# Revit family: RN 22150 Valvola di distribuzione
name_source: partatom
category: Rohrzubehör
units: mm (PartAtom-declared; Revit-internal decimal feet)

## family parameters
Arbeitsebenenbasiert = Nein
Beim Laden mit Abzugskörper schneiden = Nein
Bemaßung runder Anschluss = Durchmesser verwenden
Gemeinsam genutzt = Nein
Immer vertikal = Ja
Teiletyp = Ventil - Zerlegung in

## types (19) — shared parameters
1.010.00.2 Blattnummer der Richtlinie = 17
1.010.00.3 Ausgabedatum (Monat) der Richtlinie = 201601
1.010.00.4 Herstellername = R. Nussbaum AG
1.010.00.5 Revisionsdatum der Datei = 20190528
1.010.00.6 Webadresse des Herstellers = http://www.nussbaum.ch
1.100.00.3 Sortiernummer für Anzeigereihenfolge = 1
1.100.00.4 Produktbezeichnung = Absperrarmaturen
1.960/3L.00.8 Link (URL) = https://www.nussbaum.ch
17.700.00.4 Armaturentyp = 1
17.700.00.7 Maximale Betriebstemperatur TB [°C] = 90
17.700.00.8 Maximaler Betriebsdruck (Arbeitsdruck) ps [1.0 · 105 Pa] = 16
Connector Visibility = Nein
EnclosingSpace Visibility = Nein
Hersteller = R. Nussbauzm AG
URL = https://www.nussbaum.ch

## per-type parameters (varying)
- DN 25 3: 1.800.00.3 TGA-Nummer=00106000000000000000000000000200700000000000000001???00000; 1.810.00.3 Hersteller-Bestellnummer=22150.41; 1.810.00.4 DATANORM-Nummer=22150.41; 1.810.00.5 StLB-Nummer=622.135; 1.810.00.6 GTIN-Nummer=7612945728890; 17.700.00.30 Produktbeschreibung=22150.41, Batterieventil, ohne Anschlussverschraubung, DN=25, Rp=1; 17.700.00.5 Nennweite DN=25; 17.700.00.6 kvs-Wert [m3/h]=22.84; CONNECTOR0_DIAMETER_dX_0r=25 mm  [stored 0.082021 ft]; CONNECTOR0_dX_00=37 mm; CONNECTOR0_dX_01=20 mm; CONNECTOR0_ref_dX=20 mm; CONNECTOR1_DIAMETER_dX_0r=25 mm  [stored 0.082021 ft]; CONNECTOR1_dX_00=20 mm; CONNECTOR1_dX_01=37 mm; CONNECTOR1_ref_dX=20 mm; CONNECTOR2_DIAMETER_dZ_0r=25 mm  [stored 0.082021 ft]; CONNECTOR2_dZ_00=48 mm; CONNECTOR2_dZ_01=60 mm; CONNECTOR2_ref_dZ=48 mm; Modell=22150.41; R. Nussbaum AG 22150.40 de Visibility=Nein; R. Nussbaum AG 22150.41 de Visibility=Ja; R. Nussbaum AG 22150.42 de Visibility=Nein; R. Nussbaum AG 22150.43 de Visibility=Nein; R. Nussbaum AG 22150.44 de Visibility=Nein; R. Nussbaum AG 22150.45 de Visibility=Nein; R. Nussbaum AG 22150.46 de Visibility=Nein; R. Nussbaum AG 22150.47 de Visibility=Nein; R. Nussbaum AG 22150.48 de Visibility=Nein; R. Nussbaum AG 22150.49 de Visibility=Nein; R. Nussbaum AG 22150.50 de Visibility=Nein; R. Nussbaum AG 22150.51 de Visibility=Nein; R. Nussbaum AG 22150.52 de Visibility=Nein; R. Nussbaum AG 22150.53 de Visibility=Nein; R. Nussbaum AG 22150.54 de Visibility=Nein; R. Nussbaum AG 22150.55 de Visibility=Nein; R. Nussbaum AG 22150.56 de Visibility=Nein; R. Nussbaum AG 22150.57 de Visibility=Nein; R. Nussbaum AG 22150.58 de Visibility=Nein; Typenkommentare=Valvola di distribuzioneDN 25 3
- DN 20: 1.800.00.3 TGA-Nummer=00106000000000000000000000000200700000000000000002???00000; 1.810.00.3 Hersteller-Bestellnummer=22150.42; 1.810.00.4 DATANORM-Nummer=22150.42; 1.810.00.5 StLB-Nummer=622.116; 1.810.00.6 GTIN-Nummer=7612945728852; 17.700.00.30 Produktbeschreibung=22150.42, Batterieventil, ohne Anschlussverschraubung, DN=20, Rp=1¼; 17.700.00.5 Nennweite DN=20; 17.700.00.6 kvs-Wert [m3/h]=16; CONNECTOR0_DIAMETER_dX_0r=32 mm; CONNECTOR0_dX_00=44 mm; CONNECTOR0_dX_01=25 mm  [stored 0.082021 ft]; CONNECTOR0_ref_dX=25 mm  [stored 0.082021 ft]; CONNECTOR1_DIAMETER_dX_0r=32 mm; CONNECTOR1_dX_00=25 mm  [stored 0.082021 ft]; CONNECTOR1_dX_01=44 mm; CONNECTOR1_ref_dX=25 mm  [stored 0.082021 ft]; CONNECTOR2_DIAMETER_dZ_0r=20 mm; CONNECTOR2_dZ_00=50 mm; CONNECTOR2_dZ_01=62 mm  [stored 0.203412 ft]; CONNECTOR2_ref_dZ=50 mm; Modell=22150.42; R. Nussbaum AG 22150.40 de Visibility=Nein; R. Nussbaum AG 22150.41 de Visibility=Nein; R. Nussbaum AG 22150.42 de Visibility=Ja; R. Nussbaum AG 22150.43 de Visibility=Nein; R. Nussbaum AG 22150.44 de Visibility=Nein; R. Nussbaum AG 22150.45 de Visibility=Nein; R. Nussbaum AG 22150.46 de Visibility=Nein; R. Nussbaum AG 22150.47 de Visibility=Nein; R. Nussbaum AG 22150.48 de Visibility=Nein; R. Nussbaum AG 22150.49 de Visibility=Nein; R. Nussbaum AG 22150.50 de Visibility=Nein; R. Nussbaum AG 22150.51 de Visibility=Nein; R. Nussbaum AG 22150.52 de Visibility=Nein; R. Nussbaum AG 22150.53 de Visibility=Nein; R. Nussbaum AG 22150.54 de Visibility=Nein; R. Nussbaum AG 22150.55 de Visibility=Nein; R. Nussbaum AG 22150.56 de Visibility=Nein; R. Nussbaum AG 22150.57 de Visibility=Nein; R. Nussbaum AG 22150.58 de Visibility=Nein; Typenkommentare=Valvola di distribuzioneDN 20
- DN 25 1: 1.800.00.3 TGA-Nummer=00106000000000000000000000000200700000000000000003???00000; 1.810.00.3 Hersteller-Bestellnummer=22150.43; 1.810.00.4 DATANORM-Nummer=22150.43; 1.810.00.5 StLB-Nummer=622.136; 1.810.00.6 GTIN-Nummer=7612945728906; 17.700.00.30 Produktbeschreibung=22150.43, Batterieventil, ohne Anschlussverschraubung, DN=25, Rp=1¼; 17.700.00.5 Nennweite DN=25; 17.700.00.6 kvs-Wert [m3/h]=18.58; CONNECTOR0_DIAMETER_dX_0r=32 mm; CONNECTOR0_dX_00=44 mm; CONNECTOR0_dX_01=25 mm  [stored 0.082021 ft]; CONNECTOR0_ref_dX=25 mm  [stored 0.082021 ft]; CONNECTOR1_DIAMETER_dX_0r=32 mm; CONNECTOR1_dX_00=25 mm  [stored 0.082021 ft]; CONNECTOR1_dX_01=44 mm; CONNECTOR1_ref_dX=25 mm  [stored 0.082021 ft]; CONNECTOR2_DIAMETER_dZ_0r=25 mm  [stored 0.082021 ft]; CONNECTOR2_dZ_00=50 mm; CONNECTOR2_dZ_01=62 mm  [stored 0.203412 ft]; CONNECTOR2_ref_dZ=50 mm; Modell=22150.43; R. Nussbaum AG 22150.40 de Visibility=Nein; R. Nussbaum AG 22150.41 de Visibility=Nein; R. Nussbaum AG 22150.42 de Visibility=Nein; R. Nussbaum AG 22150.43 de Visibility=Ja; R. Nussbaum AG 22150.44 de Visibility=Nein; R. Nussbaum AG 22150.45 de Visibility=Nein; R. Nussbaum AG 22150.46 de Visibility=Nein; R. Nussbaum AG 22150.47 de Visibility=Nein; R. Nussbaum AG 22150.48 de Visibility=Nein; R. Nussbaum AG 22150.49 de Visibility=Nein; R. Nussbaum AG 22150.50 de Visibility=Nein; R. Nussbaum AG 22150.51 de Visibility=Nein; R. Nussbaum AG 22150.52 de Visibility=Nein; R. Nussbaum AG 22150.53 de Visibility=Nein; R. Nussbaum AG 22150.54 de Visibility=Nein; R. Nussbaum AG 22150.55 de Visibility=Nein; R. Nussbaum AG 22150.56 de Visibility=Nein; R. Nussbaum AG 22150.57 de Visibility=Nein; R. Nussbaum AG 22150.58 de Visibility=Nein; Typenkommentare=Valvola di distribuzioneDN 25 1
- DN 32 2: 1.800.00.3 TGA-Nummer=00106000000000000000000000000200700000000000000004???00000; 1.810.00.3 Hersteller-Bestellnummer=22150.44; 1.810.00.4 DATANORM-Nummer=22150.44; 1.810.00.5 StLB-Nummer=622.156; 1.810.00.6 GTIN-Nummer=7612945728869; 17.700.00.30 Produktbeschreibung=22150.44, Batterieventil, ohne Anschlussverschraubung, DN=32, Rp=1¼; 17.700.00.5 Nennweite DN=32; 17.700.00.6 kvs-Wert [m3/h]=43.05; CONNECTOR0_DIAMETER_dX_0r=32 mm; CONNECTOR0_dX_00=44 mm; CONNECTOR0_dX_01=25 mm  [stored 0.082021 ft]; CONNECTOR0_ref_dX=25 mm  [stored 0.082021 ft]; CONNECTOR1_DIAMETER_dX_0r=32 mm; CONNECTOR1_dX_00=25 mm  [stored 0.082021 ft]; CONNECTOR1_dX_01=44 mm; CONNECTOR1_ref_dX=25 mm  [stored 0.082021 ft]; CONNECTOR2_DIAMETER_dZ_0r=32 mm; CONNECTOR2_dZ_00=49 mm; CONNECTOR2_dZ_01=62 mm  [stored 0.203412 ft]; CONNECTOR2_ref_dZ=49 mm; Modell=22150.44; R. Nussbaum AG 22150.40 de Visibility=Nein; R. Nussbaum AG 22150.41 de Visibility=Nein; R. Nussbaum AG 22150.42 de Visibility=Nein; R. Nussbaum AG 22150.43 de Visibility=Nein; R. Nussbaum AG 22150.44 de Visibility=Ja; R. Nussbaum AG 22150.45 de Visibility=Nein; R. Nussbaum AG 22150.46 de Visibility=Nein; R. Nussbaum AG 22150.47 de Visibility=Nein; R. Nussbaum AG 22150.48 de Visibility=Nein; R. Nussbaum AG 22150.49 de Visibility=Nein; R. Nussbaum AG 22150.50 de Visibility=Nein; R. Nussbaum AG 22150.51 de Visibility=Nein; R. Nussbaum AG 22150.52 de Visibility=Nein; R. Nussbaum AG 22150.53 de Visibility=Nein; R. Nussbaum AG 22150.54 de Visibility=Nein; R. Nussbaum AG 22150.55 de Visibility=Nein; R. Nussbaum AG 22150.56 de Visibility=Nein; R. Nussbaum AG 22150.57 de Visibility=Nein; R. Nussbaum AG 22150.58 de Visibility=Nein; Typenkommentare=Valvola di distribuzioneDN 32 2
- DN 20 1: 1.800.00.3 TGA-Nummer=00106000000000000000000000000200700000000000000005???00000; 1.810.00.3 Hersteller-Bestellnummer=22150.45; 1.810.00.4 DATANORM-Nummer=22150.45; 1.810.00.5 StLB-Nummer=622.117; 1.810.00.6 GTIN-Nummer=7612945728913; 17.700.00.30 Produktbeschreibung=22150.45, Batterieventil, ohne Anschlussverschraubung, DN=20, Rp=1½; 17.700.00.5 Nennweite DN=20; 17.700.00.6 kvs-Wert [m3/h]=18; CONNECTOR0_DIAMETER_dX_0r=40 mm; CONNECTOR0_dX_00=49 mm; CONNECTOR0_dX_01=30 mm; CONNECTOR0_ref_dX=30 mm; CONNECTOR1_DIAMETER_dX_0r=40 mm; CONNECTOR1_dX_00=30 mm; CONNECTOR1_dX_01=49 mm; CONNECTOR1_ref_dX=30 mm; CONNECTOR2_DIAMETER_dZ_0r=20 mm; CONNECTOR2_dZ_00=52 mm; CONNECTOR2_dZ_01=65 mm; CONNECTOR2_ref_dZ=52 mm; Modell=22150.45; R. Nussbaum AG 22150.40 de Visibility=Nein; R. Nussbaum AG 22150.41 de Visibility=Nein; R. Nussbaum AG 22150.42 de Visibility=Nein; R. Nussbaum AG 22150.43 de Visibility=Nein; R. Nussbaum AG 22150.44 de Visibility=Nein; R. Nussbaum AG 22150.45 de Visibility=Ja; R. Nussbaum AG 22150.46 de Visibility=Nein; R. Nussbaum AG 22150.47 de Visibility=Nein; R. Nussbaum AG 22150.48 de Visibility=Nein; R. Nussbaum AG 22150.49 de Visibility=Nein; R. Nussbaum AG 22150.50 de Visibility=Nein; R. Nussbaum AG 22150.51 de Visibility=Nein; R. Nussbaum AG 22150.52 de Visibility=Nein; R. Nussbaum AG 22150.53 de Visibility=Nein; R. Nussbaum AG 22150.54 de Visibility=Nein; R. Nussbaum AG 22150.55 de Visibility=Nein; R. Nussbaum AG 22150.56 de Visibility=Nein; R. Nussbaum AG 22150.57 de Visibility=Nein; R. Nussbaum AG 22150.58 de Visibility=Nein; Typenkommentare=Valvola di distribuzioneDN 20 1
- DN 25 4: 1.800.00.3 TGA-Nummer=00106000000000000000000000000200700000000000000006???00000; 1.810.00.3 Hersteller-Bestellnummer=22150.46; 1.810.00.4 DATANORM-Nummer=22150.46; 1.810.00.5 StLB-Nummer=622.137; 1.810.00.6 GTIN-Nummer=7612945728876; 17.700.00.30 Produktbeschreibung=22150.46, Batterieventil, ohne Anschlussverschraubung, DN=25, Rp=1½; 17.700.00.5 Nennweite DN=25; 17.700.00.6 kvs-Wert [m3/h]=18; CONNECTOR0_DIAMETER_dX_0r=40 mm; CONNECTOR0_dX_00=49 mm; CONNECTOR0_dX_01=30 mm; CONNECTOR0_ref_dX=30 mm; CONNECTOR1_DIAMETER_dX_0r=40 mm; CONNECTOR1_dX_00=30 mm; CONNECTOR1_dX_01=49 mm; CONNECTOR1_ref_dX=30 mm; CONNECTOR2_DIAMETER_dZ_0r=25 mm  [stored 0.082021 ft]; CONNECTOR2_dZ_00=52 mm; CONNECTOR2_dZ_01=65 mm; CONNECTOR2_ref_dZ=52 mm; Modell=22150.46; R. Nussbaum AG 22150.40 de Visibility=Nein; R. Nussbaum AG 22150.41 de Visibility=Nein; R. Nussbaum AG 22150.42 de Visibility=Nein; R. Nussbaum AG 22150.43 de Visibility=Nein; R. Nussbaum AG 22150.44 de Visibility=Nein; R. Nussbaum AG 22150.45 de Visibility=Nein; R. Nussbaum AG 22150.46 de Visibility=Ja; R. Nussbaum AG 22150.47 de Visibility=Nein; R. Nussbaum AG 22150.48 de Visibility=Nein; R. Nussbaum AG 22150.49 de Visibility=Nein; R. Nussbaum AG 22150.50 de Visibility=Nein; R. Nussbaum AG 22150.51 de Visibility=Nein; R. Nussbaum AG 22150.52 de Visibility=Nein; R. Nussbaum AG 22150.53 de Visibility=Nein; R. Nussbaum AG 22150.54 de Visibility=Nein; R. Nussbaum AG 22150.55 de Visibility=Nein; R. Nussbaum AG 22150.56 de Visibility=Nein; R. Nussbaum AG 22150.57 de Visibility=Nein; R. Nussbaum AG 22150.58 de Visibility=Nein; Typenkommentare=Valvola di distribuzioneDN 25 4
- DN 32 1: 1.800.00.3 TGA-Nummer=00106000000000000000000000000200700000000000000007???00000; 1.810.00.3 Hersteller-Bestellnummer=22150.47; 1.810.00.4 DATANORM-Nummer=22150.47; 1.810.00.5 StLB-Nummer=622.157; 1.810.00.6 GTIN-Nummer=7612945728920; 17.700.00.30 Produktbeschreibung=22150.47, Batterieventil, ohne Anschlussverschraubung, DN=32, Rp=1½; 17.700.00.5 Nennweite DN=32; 17.700.00.6 kvs-Wert [m3/h]=36.27; CONNECTOR0_DIAMETER_dX_0r=40 mm; CONNECTOR0_dX_00=49 mm; CONNECTOR0_dX_01=30 mm; CONNECTOR0_ref_dX=30 mm; CONNECTOR1_DIAMETER_dX_0r=40 mm; CONNECTOR1_dX_00=30 mm; CONNECTOR1_dX_01=49 mm; CONNECTOR1_ref_dX=30 mm; CONNECTOR2_DIAMETER_dZ_0r=32 mm; CONNECTOR2_dZ_00=52 mm; CONNECTOR2_dZ_01=65 mm; CONNECTOR2_ref_dZ=52 mm; Modell=22150.47; R. Nussbaum AG 22150.40 de Visibility=Nein; R. Nussbaum AG 22150.41 de Visibility=Nein; R. Nussbaum AG 22150.42 de Visibility=Nein; R. Nussbaum AG 22150.43 de Visibility=Nein; R. Nussbaum AG 22150.44 de Visibility=Nein; R. Nussbaum AG 22150.45 de Visibility=Nein; R. Nussbaum AG 22150.46 de Visibility=Nein; R. Nussbaum AG 22150.47 de Visibility=Ja; R. Nussbaum AG 22150.48 de Visibility=Nein; R. Nussbaum AG 22150.49 de Visibility=Nein; R. Nussbaum AG 22150.50 de Visibility=Nein; R. Nussbaum AG 22150.51 de Visibility=Nein; R. Nussbaum AG 22150.52 de Visibility=Nein; R. Nussbaum AG 22150.53 de Visibility=Nein; R. Nussbaum AG 22150.54 de Visibility=Nein; R. Nussbaum AG 22150.55 de Visibility=Nein; R. Nussbaum AG 22150.56 de Visibility=Nein; R. Nussbaum AG 22150.57 de Visibility=Nein; R. Nussbaum AG 22150.58 de Visibility=Nein; Typenkommentare=Valvola di distribuzioneDN 32 1
- DN 40 1: 1.800.00.3 TGA-Nummer=00106000000000000000000000000200700000000000000008???00000; 1.810.00.3 Hersteller-Bestellnummer=22150.48; 1.810.00.4 DATANORM-Nummer=22150.48; 1.810.00.5 StLB-Nummer=622.217; 1.810.00.6 GTIN-Nummer=7612945726865; 17.700.00.30 Produktbeschreibung=22150.48, Batterieventil, ohne Anschlussverschraubung, DN=40, Rp=1½; 17.700.00.5 Nennweite DN=40; 17.700.00.6 kvs-Wert [m3/h]=54.13; CONNECTOR0_DIAMETER_dX_0r=40 mm; CONNECTOR0_dX_00=49 mm; CONNECTOR0_dX_01=30 mm; CONNECTOR0_ref_dX=30 mm; CONNECTOR1_DIAMETER_dX_0r=40 mm; CONNECTOR1_dX_00=30 mm; CONNECTOR1_dX_01=49 mm; CONNECTOR1_ref_dX=30 mm; CONNECTOR2_DIAMETER_dZ_0r=40 mm; CONNECTOR2_dZ_00=52 mm; CONNECTOR2_dZ_01=65 mm; CONNECTOR2_ref_dZ=52 mm; Modell=22150.48; R. Nussbaum AG 22150.40 de Visibility=Nein; R. Nussbaum AG 22150.41 de Visibility=Nein; R. Nussbaum AG 22150.42 de Visibility=Nein; R. Nussbaum AG 22150.43 de Visibility=Nein; R. Nussbaum AG 22150.44 de Visibility=Nein; R. Nussbaum AG 22150.45 de Visibility=Nein; R. Nussbaum AG 22150.46 de Visibility=Nein; R. Nussbaum AG 22150.47 de Visibility=Nein; R. Nussbaum AG 22150.48 de Visibility=Ja; R. Nussbaum AG 22150.49 de Visibility=Nein; R. Nussbaum AG 22150.50 de Visibility=Nein; R. Nussbaum AG 22150.51 de Visibility=Nein; R. Nussbaum AG 22150.52 de Visibility=Nein; R. Nussbaum AG 22150.53 de Visibility=Nein; R. Nussbaum AG 22150.54 de Visibility=Nein; R. Nussbaum AG 22150.55 de Visibility=Nein; R. Nussbaum AG 22150.56 de Visibility=Nein; R. Nussbaum AG 22150.57 de Visibility=Nein; R. Nussbaum AG 22150.58 de Visibility=Nein; Typenkommentare=Valvola di distribuzioneDN 40 1
- DN 20 3: 1.800.00.3 TGA-Nummer=00106000000000000000000000000200700000000000000009???00000; 1.810.00.3 Hersteller-Bestellnummer=22150.49; 1.810.00.4 DATANORM-Nummer=22150.49; 1.810.00.5 StLB-Nummer=622.118; 1.810.00.6 GTIN-Nummer=7612945728937; 17.700.00.30 Produktbeschreibung=22150.49, Batterieventil, ohne Anschlussverschraubung, DN=20, Rp=2; 17.700.00.5 Nennweite DN=20; 17.700.00.6 kvs-Wert [m3/h]=30; CONNECTOR0_DIAMETER_dX_0r=50 mm; CONNECTOR0_dX_00=59 mm; CONNECTOR0_dX_01=35 mm  [stored 0.114829 ft]; CONNECTOR0_ref_dX=35 mm  [stored 0.114829 ft]; CONNECTOR1_DIAMETER_dX_0r=50 mm; CONNECTOR1_dX_00=35 mm  [stored 0.114829 ft]; CONNECTOR1_dX_01=59 mm; CONNECTOR1_ref_dX=35 mm  [stored 0.114829 ft]; CONNECTOR2_DIAMETER_dZ_0r=20 mm; CONNECTOR2_dZ_00=60 mm; CONNECTOR2_dZ_01=73 mm  [stored 0.239501 ft]; CONNECTOR2_ref_dZ=60 mm; Modell=22150.49; R. Nussbaum AG 22150.40 de Visibility=Nein; R. Nussbaum AG 22150.41 de Visibility=Nein; R. Nussbaum AG 22150.42 de Visibility=Nein; R. Nussbaum AG 22150.43 de Visibility=Nein; R. Nussbaum AG 22150.44 de Visibility=Nein; R. Nussbaum AG 22150.45 de Visibility=Nein; R. Nussbaum AG 22150.46 de Visibility=Nein; R. Nussbaum AG 22150.47 de Visibility=Nein; R. Nussbaum AG 22150.48 de Visibility=Nein; R. Nussbaum AG 22150.49 de Visibility=Ja; R. Nussbaum AG 22150.50 de Visibility=Nein; R. Nussbaum AG 22150.51 de Visibility=Nein; R. Nussbaum AG 22150.52 de Visibility=Nein; R. Nussbaum AG 22150.53 de Visibility=Nein; R. Nussbaum AG 22150.54 de Visibility=Nein; R. Nussbaum AG 22150.55 de Visibility=Nein; R. Nussbaum AG 22150.56 de Visibility=Nein; R. Nussbaum AG 22150.57 de Visibility=Nein; R. Nussbaum AG 22150.58 de Visibility=Nein; Typenkommentare=Valvola di distribuzioneDN 20 3
- DN 32 3: 1.800.00.3 TGA-Nummer=00106000000000000000000000000200700000000000000010???00000; 1.810.00.3 Hersteller-Bestellnummer=22150.51; 1.810.00.4 DATANORM-Nummer=22150.51; 1.810.00.5 StLB-Nummer=622.158; 1.810.00.6 GTIN-Nummer=7612945728944; 17.700.00.30 Produktbeschreibung=22150.51, Batterieventil, ohne Anschlussverschraubung, DN=32, Rp=2; 17.700.00.5 Nennweite DN=32; 17.700.00.6 kvs-Wert [m3/h]=33.26; CONNECTOR0_DIAMETER_dX_0r=50 mm; CONNECTOR0_dX_00=59 mm; CONNECTOR0_dX_01=35 mm  [stored 0.114829 ft]; CONNECTOR0_ref_dX=35 mm  [stored 0.114829 ft]; CONNECTOR1_DIAMETER_dX_0r=50 mm; CONNECTOR1_dX_00=35 mm  [stored 0.114829 ft]; CONNECTOR1_dX_01=59 mm; CONNECTOR1_ref_dX=35 mm  [stored 0.114829 ft]; CONNECTOR2_DIAMETER_dZ_0r=32 mm; CONNECTOR2_dZ_00=60 mm; CONNECTOR2_dZ_01=73 mm  [stored 0.239501 ft]; CONNECTOR2_ref_dZ=60 mm; Modell=22150.51; R. Nussbaum AG 22150.40 de Visibility=Nein; R. Nussbaum AG 22150.41 de Visibility=Nein; R. Nussbaum AG 22150.42 de Visibility=Nein; R. Nussbaum AG 22150.43 de Visibility=Nein; R. Nussbaum AG 22150.44 de Visibility=Nein; R. Nussbaum AG 22150.45 de Visibility=Nein; R. Nussbaum AG 22150.46 de Visibility=Nein; R. Nussbaum AG 22150.47 de Visibility=Nein; R. Nussbaum AG 22150.48 de Visibility=Nein; R. Nussbaum AG 22150.49 de Visibility=Nein; R. Nussbaum AG 22150.50 de Visibility=Nein; R. Nussbaum AG 22150.51 de Visibility=Ja; R. Nussbaum AG 22150.52 de Visibility=Nein; R. Nussbaum AG 22150.53 de Visibility=Nein; R. Nussbaum AG 22150.54 de Visibility=Nein; R. Nussbaum AG 22150.55 de Visibility=Nein; R. Nussbaum AG 22150.56 de Visibility=Nein; R. Nussbaum AG 22150.57 de Visibility=Nein; R. Nussbaum AG 22150.58 de Visibility=Nein; Typenkommentare=Valvola di distribuzioneDN 32 3
- DN 40 2: 1.800.00.3 TGA-Nummer=00106000000000000000000000000200700000000000000011???00000; 1.810.00.3 Hersteller-Bestellnummer=22150.52; 1.810.00.4 DATANORM-Nummer=22150.52; 1.810.00.5 StLB-Nummer=622.218; 1.810.00.6 GTIN-Nummer=7612945726872; 17.700.00.30 Produktbeschreibung=22150.52, Batterieventil, ohne Anschlussverschraubung, DN=40, Rp=2; 17.700.00.5 Nennweite DN=40; 17.700.00.6 kvs-Wert [m3/h]=50; CONNECTOR0_DIAMETER_dX_0r=50 mm; CONNECTOR0_dX_00=59 mm; CONNECTOR0_dX_01=35 mm  [stored 0.114829 ft]; CONNECTOR0_ref_dX=35 mm  [stored 0.114829 ft]; CONNECTOR1_DIAMETER_dX_0r=50 mm; CONNECTOR1_dX_00=35 mm  [stored 0.114829 ft]; CONNECTOR1_dX_01=59 mm; CONNECTOR1_ref_dX=35 mm  [stored 0.114829 ft]; CONNECTOR2_DIAMETER_dZ_0r=40 mm; CONNECTOR2_dZ_00=60 mm; CONNECTOR2_dZ_01=73 mm  [stored 0.239501 ft]; CONNECTOR2_ref_dZ=60 mm; Modell=22150.52; R. Nussbaum AG 22150.40 de Visibility=Nein; R. Nussbaum AG 22150.41 de Visibility=Nein; R. Nussbaum AG 22150.42 de Visibility=Nein; R. Nussbaum AG 22150.43 de Visibility=Nein; R. Nussbaum AG 22150.44 de Visibility=Nein; R. Nussbaum AG 22150.45 de Visibility=Nein; R. Nussbaum AG 22150.46 de Visibility=Nein; R. Nussbaum AG 22150.47 de Visibility=Nein; R. Nussbaum AG 22150.48 de Visibility=Nein; R. Nussbaum AG 22150.49 de Visibility=Nein; R. Nussbaum AG 22150.50 de Visibility=Nein; R. Nussbaum AG 22150.51 de Visibility=Nein; R. Nussbaum AG 22150.52 de Visibility=Ja; R. Nussbaum AG 22150.53 de Visibility=Nein; R. Nussbaum AG 22150.54 de Visibility=Nein; R. Nussbaum AG 22150.55 de Visibility=Nein; R. Nussbaum AG 22150.56 de Visibility=Nein; R. Nussbaum AG 22150.57 de Visibility=Nein; R. Nussbaum AG 22150.58 de Visibility=Nein; Typenkommentare=Valvola di distribuzioneDN 40 2
- DN 50: 1.800.00.3 TGA-Nummer=00106000000000000000000000000200700000000000000012???00000; 1.810.00.3 Hersteller-Bestellnummer=22150.53; 1.810.00.4 DATANORM-Nummer=22150.53; 1.810.00.5 StLB-Nummer=622.238; 1.810.00.6 GTIN-Nummer=7612945727107; 17.700.00.30 Produktbeschreibung=22150.53, Batterieventil, ohne Anschlussverschraubung, DN=50, Rp=2; 17.700.00.5 Nennweite DN=50; 17.700.00.6 kvs-Wert [m3/h]=82.84; CONNECTOR0_DIAMETER_dX_0r=50 mm; CONNECTOR0_dX_00=59 mm; CONNECTOR0_dX_01=35 mm  [stored 0.114829 ft]; CONNECTOR0_ref_dX=35 mm  [stored 0.114829 ft]; CONNECTOR1_DIAMETER_dX_0r=50 mm; CONNECTOR1_dX_00=35 mm  [stored 0.114829 ft]; CONNECTOR1_dX_01=59 mm; CONNECTOR1_ref_dX=35 mm  [stored 0.114829 ft]; CONNECTOR2_DIAMETER_dZ_0r=50 mm; CONNECTOR2_dZ_00=60 mm; CONNECTOR2_dZ_01=73 mm  [stored 0.239501 ft]; CONNECTOR2_ref_dZ=60 mm; Modell=22150.53; R. Nussbaum AG 22150.40 de Visibility=Nein; R. Nussbaum AG 22150.41 de Visibility=Nein; R. Nussbaum AG 22150.42 de Visibility=Nein; R. Nussbaum AG 22150.43 de Visibility=Nein; R. Nussbaum AG 22150.44 de Visibility=Nein; R. Nussbaum AG 22150.45 de Visibility=Nein; R. Nussbaum AG 22150.46 de Visibility=Nein; R. Nussbaum AG 22150.47 de Visibility=Nein; R. Nussbaum AG 22150.48 de Visibility=Nein; R. Nussbaum AG 22150.49 de Visibility=Nein; R. Nussbaum AG 22150.50 de Visibility=Nein; R. Nussbaum AG 22150.51 de Visibility=Nein; R. Nussbaum AG 22150.52 de Visibility=Nein; R. Nussbaum AG 22150.53 de Visibility=Ja; R. Nussbaum AG 22150.54 de Visibility=Nein; R. Nussbaum AG 22150.55 de Visibility=Nein; R. Nussbaum AG 22150.56 de Visibility=Nein; R. Nussbaum AG 22150.57 de Visibility=Nein; R. Nussbaum AG 22150.58 de Visibility=Nein; Typenkommentare=Valvola di distribuzioneDN 50
- DN 25 2: 1.800.00.3 TGA-Nummer=00106000000000000000000000000200700000000000000013???00000; 1.810.00.3 Hersteller-Bestellnummer=22150.54; 1.810.00.4 DATANORM-Nummer=22150.54; 1.810.00.5 StLB-Nummer=622.141; 1.810.00.6 GTIN-Nummer=7612945726889; 17.700.00.30 Produktbeschreibung=22150.54, Batterieventil, ohne Anschlussverschraubung, DN=25, Rp=2½; 17.700.00.5 Nennweite DN=25; 17.700.00.6 kvs-Wert [m3/h]=38; CONNECTOR0_DIAMETER_dX_0r=65 mm; CONNECTOR0_dX_00=62 mm  [stored 0.203412 ft]; CONNECTOR0_dX_01=35 mm  [stored 0.114829 ft]; CONNECTOR0_ref_dX=35 mm  [stored 0.114829 ft]; CONNECTOR1_DIAMETER_dX_0r=65 mm; CONNECTOR1_dX_00=35 mm  [stored 0.114829 ft]; CONNECTOR1_dX_01=62 mm  [stored 0.203412 ft]; CONNECTOR1_ref_dX=35 mm  [stored 0.114829 ft]; CONNECTOR2_DIAMETER_dZ_0r=25 mm  [stored 0.082021 ft]; CONNECTOR2_dZ_00=70 mm; CONNECTOR2_dZ_01=83 mm; CONNECTOR2_ref_dZ=70 mm; Modell=22150.54; R. Nussbaum AG 22150.40 de Visibility=Nein; R. Nussbaum AG 22150.41 de Visibility=Nein; R. Nussbaum AG 22150.42 de Visibility=Nein; R. Nussbaum AG 22150.43 de Visibility=Nein; R. Nussbaum AG 22150.44 de Visibility=Nein; R. Nussbaum AG 22150.45 de Visibility=Nein; R. Nussbaum AG 22150.46 de Visibility=Nein; R. Nussbaum AG 22150.47 de Visibility=Nein; R. Nussbaum AG 22150.48 de Visibility=Nein; R. Nussbaum AG 22150.49 de Visibility=Nein; R. Nussbaum AG 22150.50 de Visibility=Nein; R. Nussbaum AG 22150.51 de Visibility=Nein; R. Nussbaum AG 22150.52 de Visibility=Nein; R. Nussbaum AG 22150.53 de Visibility=Nein; R. Nussbaum AG 22150.54 de Visibility=Ja; R. Nussbaum AG 22150.55 de Visibility=Nein; R. Nussbaum AG 22150.56 de Visibility=Nein; R. Nussbaum AG 22150.57 de Visibility=Nein; R. Nussbaum AG 22150.58 de Visibility=Nein; Typenkommentare=Valvola di distribuzioneDN 25 2
- DN 32: 1.800.00.3 TGA-Nummer=00106000000000000000000000000200700000000000000014???00000; 1.810.00.3 Hersteller-Bestellnummer=22150.55; 1.810.00.4 DATANORM-Nummer=22150.55; 1.810.00.5 StLB-Nummer=622.161; 1.810.00.6 GTIN-Nummer=7612945727114; 17.700.00.30 Produktbeschreibung=22150.55, Batterieventil, ohne Anschlussverschraubung, DN=32, Rp=2½; 17.700.00.5 Nennweite DN=32; 17.700.00.6 kvs-Wert [m3/h]=33.56; CONNECTOR0_DIAMETER_dX_0r=65 mm; CONNECTOR0_dX_00=62 mm  [stored 0.203412 ft]; CONNECTOR0_dX_01=35 mm  [stored 0.114829 ft]; CONNECTOR0_ref_dX=35 mm  [stored 0.114829 ft]; CONNECTOR1_DIAMETER_dX_0r=65 mm; CONNECTOR1_dX_00=35 mm  [stored 0.114829 ft]; CONNECTOR1_dX_01=62 mm  [stored 0.203412 ft]; CONNECTOR1_ref_dX=35 mm  [stored 0.114829 ft]; CONNECTOR2_DIAMETER_dZ_0r=32 mm; CONNECTOR2_dZ_00=70 mm; CONNECTOR2_dZ_01=83 mm; CONNECTOR2_ref_dZ=70 mm; Modell=22150.55; R. Nussbaum AG 22150.40 de Visibility=Nein; R. Nussbaum AG 22150.41 de Visibility=Nein; R. Nussbaum AG 22150.42 de Visibility=Nein; R. Nussbaum AG 22150.43 de Visibility=Nein; R. Nussbaum AG 22150.44 de Visibility=Nein; R. Nussbaum AG 22150.45 de Visibility=Nein; R. Nussbaum AG 22150.46 de Visibility=Nein; R. Nussbaum AG 22150.47 de Visibility=Nein; R. Nussbaum AG 22150.48 de Visibility=Nein; R. Nussbaum AG 22150.49 de Visibility=Nein; R. Nussbaum AG 22150.50 de Visibility=Nein; R. Nussbaum AG 22150.51 de Visibility=Nein; R. Nussbaum AG 22150.52 de Visibility=Nein; R. Nussbaum AG 22150.53 de Visibility=Nein; R. Nussbaum AG 22150.54 de Visibility=Nein; R. Nussbaum AG 22150.55 de Visibility=Ja; R. Nussbaum AG 22150.56 de Visibility=Nein; R. Nussbaum AG 22150.57 de Visibility=Nein; R. Nussbaum AG 22150.58 de Visibility=Nein; Typenkommentare=Valvola di distribuzioneDN 32
- DN 40: 1.800.00.3 TGA-Nummer=00106000000000000000000000000200700000000000000015???00000; 1.810.00.3 Hersteller-Bestellnummer=22150.56; 1.810.00.4 DATANORM-Nummer=22150.56; 1.810.00.5 StLB-Nummer=622.221; 1.810.00.6 GTIN-Nummer=7612945726896; 17.700.00.30 Produktbeschreibung=22150.56, Batterieventil, ohne Anschlussverschraubung, DN=40, Rp=2½; 17.700.00.5 Nennweite DN=40; 17.700.00.6 kvs-Wert [m3/h]=55; CONNECTOR0_DIAMETER_dX_0r=65 mm; CONNECTOR0_dX_00=62 mm  [stored 0.203412 ft]; CONNECTOR0_dX_01=35 mm  [stored 0.114829 ft]; CONNECTOR0_ref_dX=35 mm  [stored 0.114829 ft]; CONNECTOR1_DIAMETER_dX_0r=65 mm; CONNECTOR1_dX_00=35 mm  [stored 0.114829 ft]; CONNECTOR1_dX_01=62 mm  [stored 0.203412 ft]; CONNECTOR1_ref_dX=35 mm  [stored 0.114829 ft]; CONNECTOR2_DIAMETER_dZ_0r=40 mm; CONNECTOR2_dZ_00=70 mm; CONNECTOR2_dZ_01=83 mm; CONNECTOR2_ref_dZ=70 mm; Modell=22150.56; R. Nussbaum AG 22150.40 de Visibility=Nein; R. Nussbaum AG 22150.41 de Visibility=Nein; R. Nussbaum AG 22150.42 de Visibility=Nein; R. Nussbaum AG 22150.43 de Visibility=Nein; R. Nussbaum AG 22150.44 de Visibility=Nein; R. Nussbaum AG 22150.45 de Visibility=Nein; R. Nussbaum AG 22150.46 de Visibility=Nein; R. Nussbaum AG 22150.47 de Visibility=Nein; R. Nussbaum AG 22150.48 de Visibility=Nein; R. Nussbaum AG 22150.49 de Visibility=Nein; R. Nussbaum AG 22150.50 de Visibility=Nein; R. Nussbaum AG 22150.51 de Visibility=Nein; R. Nussbaum AG 22150.52 de Visibility=Nein; R. Nussbaum AG 22150.53 de Visibility=Nein; R. Nussbaum AG 22150.54 de Visibility=Nein; R. Nussbaum AG 22150.55 de Visibility=Nein; R. Nussbaum AG 22150.56 de Visibility=Ja; R. Nussbaum AG 22150.57 de Visibility=Nein; R. Nussbaum AG 22150.58 de Visibility=Nein; Typenkommentare=Valvola di distribuzioneDN 40
- DN 50 1: 1.800.00.3 TGA-Nummer=00106000000000000000000000000200700000000000000016???00000; 1.810.00.3 Hersteller-Bestellnummer=22150.57; 1.810.00.4 DATANORM-Nummer=22150.57; 1.810.00.5 StLB-Nummer=622.241; 1.810.00.6 GTIN-Nummer=7612945727121; 17.700.00.30 Produktbeschreibung=22150.57, Batterieventil, ohne Anschlussverschraubung, DN=50, Rp=2½; 17.700.00.5 Nennweite DN=50; 17.700.00.6 kvs-Wert [m3/h]=72.18; CONNECTOR0_DIAMETER_dX_0r=65 mm; CONNECTOR0_dX_00=62 mm  [stored 0.203412 ft]; CONNECTOR0_dX_01=35 mm  [stored 0.114829 ft]; CONNECTOR0_ref_dX=35 mm  [stored 0.114829 ft]; CONNECTOR1_DIAMETER_dX_0r=65 mm; CONNECTOR1_dX_00=35 mm  [stored 0.114829 ft]; CONNECTOR1_dX_01=62 mm  [stored 0.203412 ft]; CONNECTOR1_ref_dX=35 mm  [stored 0.114829 ft]; CONNECTOR2_DIAMETER_dZ_0r=50 mm; CONNECTOR2_dZ_00=70 mm; CONNECTOR2_dZ_01=83 mm; CONNECTOR2_ref_dZ=70 mm; Modell=22150.57; R. Nussbaum AG 22150.40 de Visibility=Nein; R. Nussbaum AG 22150.41 de Visibility=Nein; R. Nussbaum AG 22150.42 de Visibility=Nein; R. Nussbaum AG 22150.43 de Visibility=Nein; R. Nussbaum AG 22150.44 de Visibility=Nein; R. Nussbaum AG 22150.45 de Visibility=Nein; R. Nussbaum AG 22150.46 de Visibility=Nein; R. Nussbaum AG 22150.47 de Visibility=Nein; R. Nussbaum AG 22150.48 de Visibility=Nein; R. Nussbaum AG 22150.49 de Visibility=Nein; R. Nussbaum AG 22150.50 de Visibility=Nein; R. Nussbaum AG 22150.51 de Visibility=Nein; R. Nussbaum AG 22150.52 de Visibility=Nein; R. Nussbaum AG 22150.53 de Visibility=Nein; R. Nussbaum AG 22150.54 de Visibility=Nein; R. Nussbaum AG 22150.55 de Visibility=Nein; R. Nussbaum AG 22150.56 de Visibility=Nein; R. Nussbaum AG 22150.57 de Visibility=Ja; R. Nussbaum AG 22150.58 de Visibility=Nein; Typenkommentare=Valvola di distribuzioneDN 50 1
- DN 25: 1.800.00.3 TGA-Nummer=00106000000000000000000000000200700000000000000017???00000; 1.810.00.3 Hersteller-Bestellnummer=22150.5; 1.810.00.4 DATANORM-Nummer=22150.5; 1.810.00.5 StLB-Nummer=622.138; 1.810.00.6 GTIN-Nummer=7612945728883; 17.700.00.30 Produktbeschreibung=22150.50, Batterieventil, ohne Anschlussverschraubung, DN=25, Rp=2; 17.700.00.5 Nennweite DN=25; 17.700.00.6 kvs-Wert [m3/h]=31; CONNECTOR0_DIAMETER_dX_0r=50 mm; CONNECTOR0_dX_00=59 mm; CONNECTOR0_dX_01=35 mm  [stored 0.114829 ft]; CONNECTOR0_ref_dX=35 mm  [stored 0.114829 ft]; CONNECTOR1_DIAMETER_dX_0r=50 mm; CONNECTOR1_dX_00=35 mm  [stored 0.114829 ft]; CONNECTOR1_dX_01=59 mm; CONNECTOR1_ref_dX=35 mm  [stored 0.114829 ft]; CONNECTOR2_DIAMETER_dZ_0r=25 mm  [stored 0.082021 ft]; CONNECTOR2_dZ_00=60 mm; CONNECTOR2_dZ_01=73 mm  [stored 0.239501 ft]; CONNECTOR2_ref_dZ=60 mm; Modell=22150.5; R. Nussbaum AG 22150.40 de Visibility=Nein; R. Nussbaum AG 22150.41 de Visibility=Nein; R. Nussbaum AG 22150.42 de Visibility=Nein; R. Nussbaum AG 22150.43 de Visibility=Nein; R. Nussbaum AG 22150.44 de Visibility=Nein; R. Nussbaum AG 22150.45 de Visibility=Nein; R. Nussbaum AG 22150.46 de Visibility=Nein; R. Nussbaum AG 22150.47 de Visibility=Nein; R. Nussbaum AG 22150.48 de Visibility=Nein; R. Nussbaum AG 22150.49 de Visibility=Nein; R. Nussbaum AG 22150.50 de Visibility=Ja; R. Nussbaum AG 22150.51 de Visibility=Nein; R. Nussbaum AG 22150.52 de Visibility=Nein; R. Nussbaum AG 22150.53 de Visibility=Nein; R. Nussbaum AG 22150.54 de Visibility=Nein; R. Nussbaum AG 22150.55 de Visibility=Nein; R. Nussbaum AG 22150.56 de Visibility=Nein; R. Nussbaum AG 22150.57 de Visibility=Nein; R. Nussbaum AG 22150.58 de Visibility=Nein; Typenkommentare=Valvola di distribuzioneDN 25
- DN 65: 1.800.00.3 TGA-Nummer=00106000000000000000000000000200700000000000000018???00000; 1.810.00.3 Hersteller-Bestellnummer=22150.58; 1.810.00.4 DATANORM-Nummer=22150.58; 1.810.00.5 StLB-Nummer=622.251; 1.810.00.6 GTIN-Nummer=7612945726186; 17.700.00.30 Produktbeschreibung=22150.58, Batterieventil, ohne Anschlussverschraubung, DN=65, Rp=2½; 17.700.00.5 Nennweite DN=65; 17.700.00.6 kvs-Wert [m3/h]=125.25; CONNECTOR0_DIAMETER_dX_0r=65 mm; CONNECTOR0_dX_00=70 mm; CONNECTOR0_dX_01=60 mm; CONNECTOR0_ref_dX=60 mm; CONNECTOR1_DIAMETER_dX_0r=65 mm; CONNECTOR1_dX_00=60 mm; CONNECTOR1_dX_01=70 mm; CONNECTOR1_ref_dX=60 mm; CONNECTOR2_DIAMETER_dZ_0r=129 mm; CONNECTOR2_dZ_00=75 mm; CONNECTOR2_dZ_01=59 mm; CONNECTOR2_ref_dZ=59 mm; Modell=22150.58; R. Nussbaum AG 22150.40 de Visibility=Nein; R. Nussbaum AG 22150.41 de Visibility=Nein; R. Nussbaum AG 22150.42 de Visibility=Nein; R. Nussbaum AG 22150.43 de Visibility=Nein; R. Nussbaum AG 22150.44 de Visibility=Nein; R. Nussbaum AG 22150.45 de Visibility=Nein; R. Nussbaum AG 22150.46 de Visibility=Nein; R. Nussbaum AG 22150.47 de Visibility=Nein; R. Nussbaum AG 22150.48 de Visibility=Nein; R. Nussbaum AG 22150.49 de Visibility=Nein; R. Nussbaum AG 22150.50 de Visibility=Nein; R. Nussbaum AG 22150.51 de Visibility=Nein; R. Nussbaum AG 22150.52 de Visibility=Nein; R. Nussbaum AG 22150.53 de Visibility=Nein; R. Nussbaum AG 22150.54 de Visibility=Nein; R. Nussbaum AG 22150.55 de Visibility=Nein; R. Nussbaum AG 22150.56 de Visibility=Nein; R. Nussbaum AG 22150.57 de Visibility=Nein; R. Nussbaum AG 22150.58 de Visibility=Ja; Typenkommentare=Valvola di distribuzioneDN 65
- DN 20 2: 1.800.00.3 TGA-Nummer=00106000000000000000000000000200700000000000000019???00000; 1.810.00.3 Hersteller-Bestellnummer=22150.4; 1.810.00.4 DATANORM-Nummer=22150.4; 1.810.00.5 StLB-Nummer=622.115; 1.810.00.6 GTIN-Nummer=7612945728845; 17.700.00.30 Produktbeschreibung=22150.40, Batterieventil, ohne Anschlussverschraubung, DN=20, Rp=1; 17.700.00.5 Nennweite DN=20; 17.700.00.6 kvs-Wert [m3/h]=12; CONNECTOR0_DIAMETER_dX_0r=25 mm  [stored 0.082021 ft]; CONNECTOR0_dX_00=37 mm; CONNECTOR0_dX_01=20 mm; CONNECTOR0_ref_dX=20 mm; CONNECTOR1_DIAMETER_dX_0r=25 mm  [stored 0.082021 ft]; CONNECTOR1_dX_00=20 mm; CONNECTOR1_dX_01=37 mm; CONNECTOR1_ref_dX=20 mm; CONNECTOR2_DIAMETER_dZ_0r=20 mm; CONNECTOR2_dZ_00=48 mm; CONNECTOR2_dZ_01=60 mm; CONNECTOR2_ref_dZ=48 mm; Modell=22150.4; R. Nussbaum AG 22150.40 de Visibility=Ja; R. Nussbaum AG 22150.41 de Visibility=Nein; R. Nussbaum AG 22150.42 de Visibility=Nein; R. Nussbaum AG 22150.43 de Visibility=Nein; R. Nussbaum AG 22150.44 de Visibility=Nein; R. Nussbaum AG 22150.45 de Visibility=Nein; R. Nussbaum AG 22150.46 de Visibility=Nein; R. Nussbaum AG 22150.47 de Visibility=Nein; R. Nussbaum AG 22150.48 de Visibility=Nein; R. Nussbaum AG 22150.49 de Visibility=Nein; R. Nussbaum AG 22150.50 de Visibility=Nein; R. Nussbaum AG 22150.51 de Visibility=Nein; R. Nussbaum AG 22150.52 de Visibility=Nein; R. Nussbaum AG 22150.53 de Visibility=Nein; R. Nussbaum AG 22150.54 de Visibility=Nein; R. Nussbaum AG 22150.55 de Visibility=Nein; R. Nussbaum AG 22150.56 de Visibility=Nein; R. Nussbaum AG 22150.57 de Visibility=Nein; R. Nussbaum AG 22150.58 de Visibility=Nein; Typenkommentare=Valvola di distribuzioneDN 20 2

note: [stored X ft] marks values corroborated as IEEE doubles in the binary element streams (Revit-internal decimal feet)

## geometry (parser evidence)
native form markers: Sweep x2
no freeform markers — native parametric forms only
